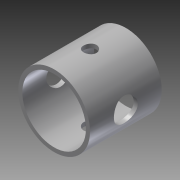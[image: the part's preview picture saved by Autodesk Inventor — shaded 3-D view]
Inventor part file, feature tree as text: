
AUTODESK INVENTOR PART (.ipt)
format: ipt  version: 2013 (Build 170138000, 138)  size: 122,368 bytes
history: native  units: in
note: dims shown in document units (in); Inventor stores cm internally (conversion verified against a paired STEP export)
features: sketch x3, plane x2, hole x2, extrude x1
ambient origin geometry x8: Origin, YZ Plane, XZ Plane, XY Plane, X Axis, Y Axis, Z Axis, Center Point
bodies: Solid1 (feature_tree)
feature tree (8):
  extrude  "Extrusion1"  Depth=1.33in
  plane  "Work Plane1"
  hole  "Hole1"  [1 undecoded]
  plane  "Work Plane2"
  hole  "Hole2"  [1 undecoded]
  sketch  "Sketch1"  dims[d0=1.5in d2=1.33in]
  sketch  "Sketch2"  dims[d3=1.5in d4=0.0in]
  sketch  "Sketch3"  dims[d5=0.5in d6=0.75in d7=0.375in d8=0.25in d9=0.5635in d10=1.0in d11=0.8108in d12=0.27in d13=0.75in d14=0.375in d15=0.25in d16=0.5635in d17=1.0in d18=0.8108in]
note: 2 required parameter values undecoded (feature->parameter linkage not recoverable at this tier; creation-order binding heuristic only, values carry confidence <= 0.55)
